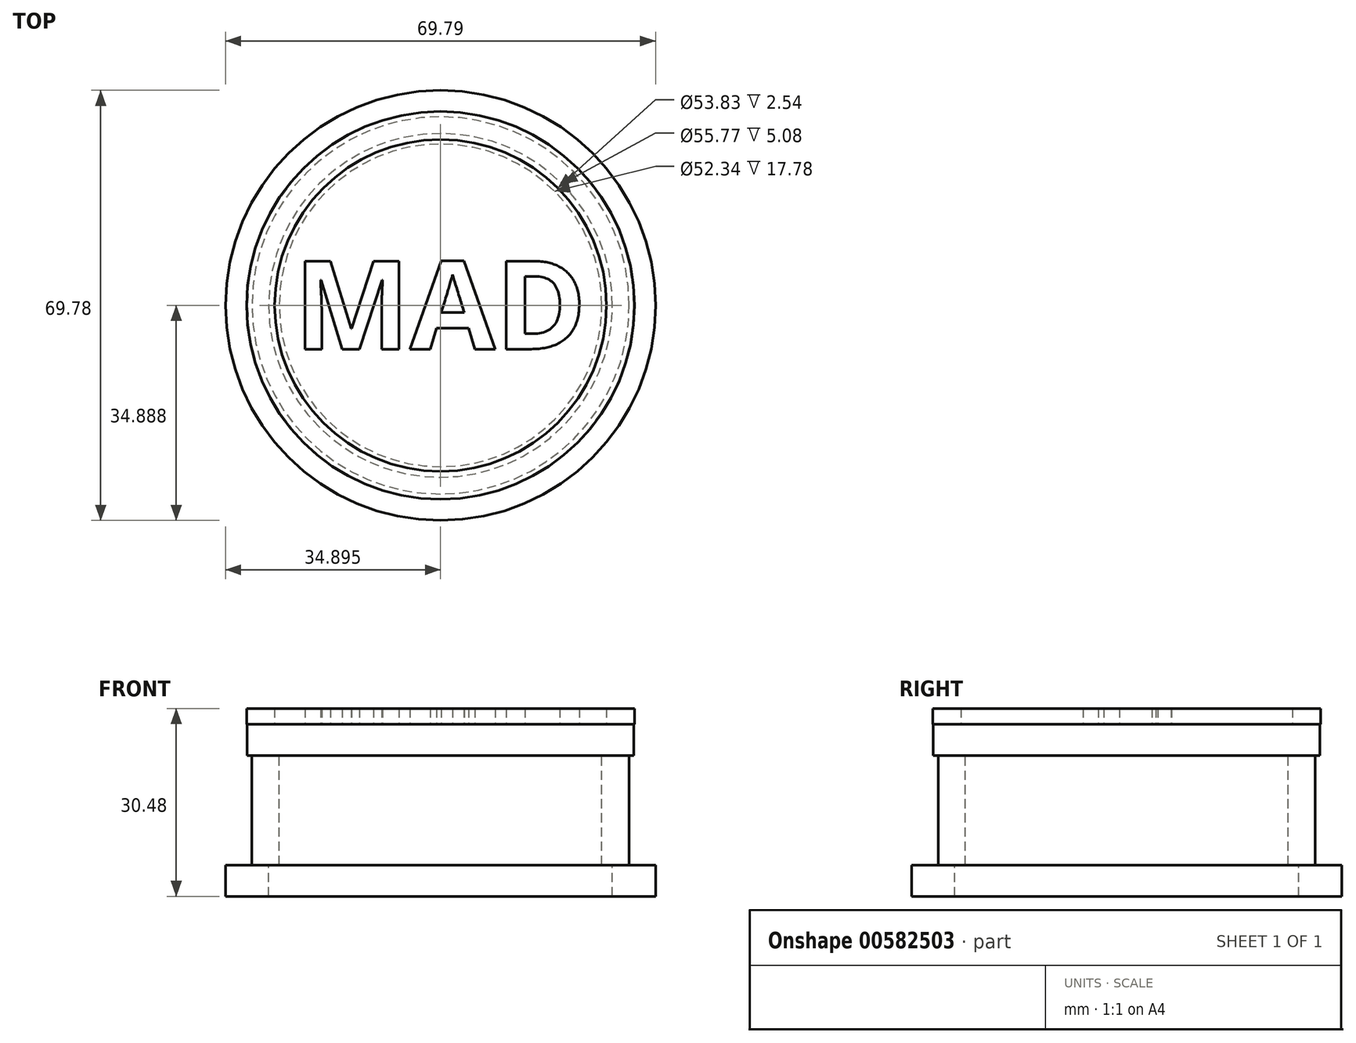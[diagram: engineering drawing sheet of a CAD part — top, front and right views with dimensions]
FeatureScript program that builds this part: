
annotation { "Feature Type Name" : "Feature", "Feature Type Description" : "" }
export const myFeature = defineFeature(function(context is Context, id is Id, definition is map)
    precondition{}
    {
        {
            var Q0;
            Q0=qCreatedBy(makeId("Top.planeOp"),FACE);
            var sketch = newSketch(context, id + "F0", { "sketchPlane" : qUnion([Q0])});
            skCircle(sketch, "E0", {"center": v(-34.36, 44.13) * mm, "radius": 31.37 * mm});
            skSolve(sketch);
        }
        {
            var Q0;
            Q0 = qSketchRegion(id + "F0", true);
            extrude(context, id + "F1", {"entities" : qUnion([Q0]), "depth" : 5.08 * mm, "offsetDistance" : 25.4 * mm});
        }
        {
            var Q0;
            Q0=makeQuery(id+"F1.opExtrude","CAP_FACE",FACE,{"disambiguationData":[OSD([sQuery(id+"F0.wireOp",EDGE,"E0")])],"isStart":false});
            var sketch = newSketch(context, id + "F2", { "sketchPlane" : qUnion([Q0])});
            skText(sketch, "E1", { "text": "MAD", "fontName": "OpenSans-Bold.ttf"});
            const initialGuessF2  = {"E1": [-0.05815, 0.03704, 1, 0, 0.0144]};
            skSetInitialGuess(sketch, initialGuessF2);
            skSolve(sketch);
        }
        {
            var Q0;
            Q0 = qSketchRegion(id + "F2", true);
            extrude(context, id + "F3", {"entities" : qUnion([Q0]), "operationType" : NewBodyOperationType.ADD, "depth" : 2.54 * mm, "offsetDistance" : 25.4 * mm});
        }
        {
            var Q0;
            {var subQ0=sQuery(id+"F0.wireOp",EDGE,"E0");Q0=makeQuery(id+"F3.boolean.opBoolean","SPLIT",FACE,{"disambiguationData":[TD([makeQuery(id+"F1.opExtrude","SWEPT_FACE",FACE,{"disambiguationData":[OSD([subQ0])]})])],"derivedFrom":makeQuery(id+"F1.opExtrude","CAP_FACE",FACE,{"disambiguationData":[OSD([subQ0])],"isStart":false})});}
            var sketch = newSketch(context, id + "F4", { "sketchPlane" : qUnion([Q0])});
            skCircle(sketch, "E2", {"center": v(-34.36, 44.13) * mm, "radius": 31.46 * mm});
            skCircle(sketch, "E3", {"center": v(-34.36, 44.13) * mm, "radius": 26.92 * mm});
            skSolve(sketch);
        }
        {
            var Q0;
            Q0 = qSketchRegion(id + "F4", true);
            extrude(context, id + "F5", {"entities" : qUnion([Q0]), "operationType" : NewBodyOperationType.ADD, "depth" : 2.54 * mm, "offsetDistance" : 25.4 * mm});
        }
        {
            var Q0;
            Q0=makeQuery(id+"F1.opExtrude","CAP_FACE",FACE,{"disambiguationData":[OSD([sQuery(id+"F0.wireOp",EDGE,"E0")])],"isStart":true});
            var sketch = newSketch(context, id + "F6", { "sketchPlane" : qUnion([Q0])});
            skCircle(sketch, "E4", {"center": v(-34.36, -44.13) * mm, "radius": 30.6 * mm});
            skCircle(sketch, "E5", {"center": v(-34.36, -44.13) * mm, "radius": 26.17 * mm});
            skSolve(sketch);
        }
        {
            var Q0;
            Q0 = qSketchRegion(id + "F6", true);
            extrude(context, id + "F7", {"entities" : qUnion([Q0]), "operationType" : NewBodyOperationType.ADD, "depth" : 17.78 * mm, "offsetDistance" : 25.4 * mm});
        }
        {
            var Q0;
            Q0=makeQuery(id+"F7.opExtrude","CAP_FACE",FACE,{"disambiguationData":[OSD([sQuery(id+"F6.wireOp",EDGE,"E4"),sQuery(id+"F6.wireOp",EDGE,"E5")])],"isStart":false});
            var sketch = newSketch(context, id + "F8", { "sketchPlane" : qUnion([Q0])});
            skCircle(sketch, "E6", {"center": v(-34.36, -44.13) * mm, "radius": 34.9 * mm});
            skCircle(sketch, "E7", {"center": v(-34.36, -44.13) * mm, "radius": 27.89 * mm});
            skSolve(sketch);
        }
        {
            var Q0;
            Q0 = qSketchRegion(id + "F8", true);
            extrude(context, id + "F9", {"entities" : qUnion([Q0]), "operationType" : NewBodyOperationType.ADD, "depth" : 5.08 * mm, "offsetDistance" : 25.4 * mm});
        }
    });
